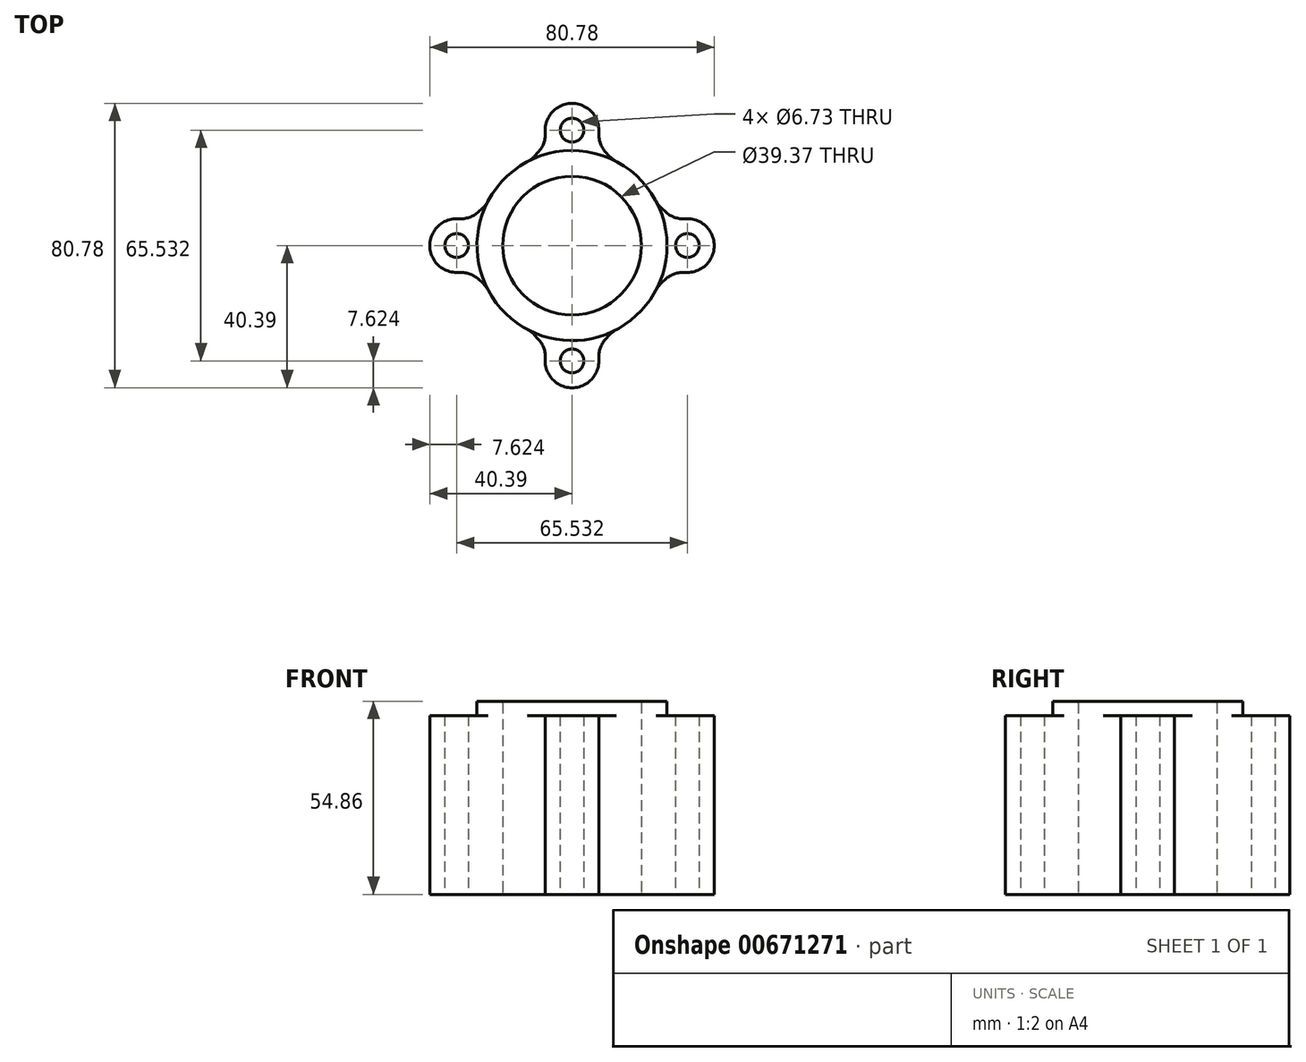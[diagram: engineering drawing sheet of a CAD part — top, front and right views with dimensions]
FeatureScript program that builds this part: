
annotation { "Feature Type Name" : "Feature", "Feature Type Description" : "" }
export const myFeature = defineFeature(function(context is Context, id is Id, definition is map)
    precondition{}
    {
        {
            var Q0;
            Q0=qCreatedBy(makeId("Top.planeOp"),FACE);
            var sketch = newSketch(context, id + "F0", { "sketchPlane" : qUnion([Q0])});
            skCircle(sketch, "E0", {"center": v(0, 0) * mm, "radius": 20.32 * mm});
            skCircle(sketch, "E1", {"center": v(0, 0) * mm, "radius": 26.99 * mm});
            skPoint(sketch, "E2", {"position": v(-32.77, 0) * mm});
            skPoint(sketch, "E3", {"position": v(32.77, 0) * mm});
            skPoint(sketch, "E4", {"position": v(0, 32.77) * mm});
            skPoint(sketch, "E5", {"position": v(0, -32.77) * mm});
            skCircle(sketch, "E6", {"center": v(-32.77, 0) * mm, "radius": 3.37 * mm});
            skCircle(sketch, "E7", {"center": v(32.77, 0) * mm, "radius": 3.37 * mm});
            skCircle(sketch, "E8", {"center": v(0, -32.77) * mm, "radius": 3.37 * mm});
            skCircle(sketch, "E9", {"center": v(0, 32.77) * mm, "radius": 3.37 * mm});
            skCircle(sketch, "E10", {"center": v(0, 32.77) * mm, "radius": 7.62 * mm});
            skCircle(sketch, "E11", {"center": v(-32.77, 0) * mm, "radius": 7.62 * mm});
            skCircle(sketch, "E12", {"center": v(0, -32.77) * mm, "radius": 7.62 * mm});
            skCircle(sketch, "E13", {"center": v(32.77, 0) * mm, "radius": 7.62 * mm});
            skPoint(sketch, "E14", {"position": v(6.87, 29.47) * mm});
            skPoint(sketch, "E15", {"position": v(11.55, 24.4) * mm});
            skPoint(sketch, "E16", {"position": v(24.4, 11.55) * mm});
            skPoint(sketch, "E17", {"position": v(29.47, 6.87) * mm});
            skLineSegment(sketch, "E18", {"start": v(6.87, 29.47) * mm, "end": v(11.55, 24.4) * mm});
            skLineSegment(sketch, "E19", {"start": v(24.4, 11.55) * mm, "end": v(29.47, 6.87) * mm});
            skPoint(sketch, "E20", {"position": v(-6.87, 29.47) * mm});
            skPoint(sketch, "E21", {"position": v(-11.55, 24.4) * mm});
            skPoint(sketch, "E22", {"position": v(-24.4, 11.55) * mm});
            skPoint(sketch, "E23", {"position": v(-29.47, 6.87) * mm});
            skPoint(sketch, "E24", {"position": v(-29.47, -6.87) * mm});
            skPoint(sketch, "E25", {"position": v(-24.4, -11.55) * mm});
            skPoint(sketch, "E26", {"position": v(-11.55, -24.4) * mm});
            skPoint(sketch, "E27", {"position": v(-6.87, -29.47) * mm});
            skPoint(sketch, "E28", {"position": v(6.87, -29.47) * mm});
            skPoint(sketch, "E29", {"position": v(11.55, -24.4) * mm});
            skPoint(sketch, "E30", {"position": v(24.4, -11.55) * mm});
            skPoint(sketch, "E31", {"position": v(29.47, -6.87) * mm});
            skLineSegment(sketch, "E32", {"start": v(-29.47, -6.87) * mm, "end": v(-24.4, -11.55) * mm});
            skLineSegment(sketch, "E33", {"start": v(-29.47, 6.87) * mm, "end": v(-24.4, 11.55) * mm});
            skLineSegment(sketch, "E34", {"start": v(-11.55, -24.4) * mm, "end": v(-6.87, -29.47) * mm});
            skLineSegment(sketch, "E35", {"start": v(6.87, -29.47) * mm, "end": v(11.55, -24.4) * mm});
            skLineSegment(sketch, "E36", {"start": v(24.4, -11.55) * mm, "end": v(29.47, -6.87) * mm});
            skLineSegment(sketch, "E37", {"start": v(-11.55, 24.4) * mm, "end": v(-6.87, 29.47) * mm});
            skSolve(sketch);
        }
        {
            var Q0;
            {var subQ0=sQuery(id+"F0.wireOp",EDGE,"E37");Q0=makeQuery(id+"F0.imprint","IMPRINT",FACE,{"disambiguationData":[TD([[makeQuery(id+"F0.imprint","IMPRINT",EDGE,{"derivedFrom":subQ0}),-1.0]])]});}
            var Q1;
            {var subQ0=sQuery(id+"F0.wireOp",EDGE,"E18");Q1=makeQuery(id+"F0.imprint","IMPRINT",FACE,{"disambiguationData":[TD([[makeQuery(id+"F0.imprint","IMPRINT",EDGE,{"derivedFrom":subQ0}),-1.0]])]});}
            var Q2;
            Q2=makeQuery(id+"F0.imprint","IMPRINT",FACE,{"disambiguationData":[TD([[makeQuery(id+"F0.imprint","IMPRINT",EDGE,{"derivedFrom":sQuery(id+"F0.wireOp",EDGE,"E9")}),-1.0]])]});
            var Q3;
            {var subQ0=sQuery(id+"F0.wireOp",EDGE,"E10");var subQ1=sQuery(id+"F0.wireOp",EDGE,"E1");var subQ2=makeQuery(id+"F0.imprint","INTERSECT",VERTEX,{"disambiguationData":[OD(0.0)],"derivedFrom":[subQ1,subQ0]});Q3=makeQuery(id+"F0.imprint","IMPRINT",FACE,{"disambiguationData":[TD([[makeQuery(id+"F0.imprint","IMPRINT",EDGE,{"disambiguationData":[TD([[subQ2,-1.0]])],"derivedFrom":subQ1}),1.0]])]});}
            var Q4;
            {var subQ0=sQuery(id+"F0.wireOp",EDGE,"E33");Q4=makeQuery(id+"F0.imprint","IMPRINT",FACE,{"disambiguationData":[TD([[makeQuery(id+"F0.imprint","IMPRINT",EDGE,{"derivedFrom":subQ0}),-1.0]])]});}
            var Q5;
            Q5=makeQuery(id+"F0.imprint","IMPRINT",FACE,{"disambiguationData":[TD([[makeQuery(id+"F0.imprint","IMPRINT",EDGE,{"derivedFrom":sQuery(id+"F0.wireOp",EDGE,"E6")}),-1.0]])]});
            var Q6;
            {var subQ0=sQuery(id+"F0.wireOp",EDGE,"E11");var subQ1=sQuery(id+"F0.wireOp",EDGE,"E1");var subQ2=makeQuery(id+"F0.imprint","INTERSECT",VERTEX,{"disambiguationData":[OD(0.0)],"derivedFrom":[subQ1,subQ0]});Q6=makeQuery(id+"F0.imprint","IMPRINT",FACE,{"disambiguationData":[TD([[makeQuery(id+"F0.imprint","IMPRINT",EDGE,{"disambiguationData":[TD([[subQ2,-1.0]])],"derivedFrom":subQ1}),1.0]])]});}
            var Q7;
            {var subQ0=sQuery(id+"F0.wireOp",EDGE,"E32");Q7=makeQuery(id+"F0.imprint","IMPRINT",FACE,{"disambiguationData":[TD([[makeQuery(id+"F0.imprint","IMPRINT",EDGE,{"derivedFrom":subQ0}),1.0]])]});}
            var Q8;
            {var subQ0=sQuery(id+"F0.wireOp",EDGE,"E34");Q8=makeQuery(id+"F0.imprint","IMPRINT",FACE,{"disambiguationData":[TD([[makeQuery(id+"F0.imprint","IMPRINT",EDGE,{"derivedFrom":subQ0}),1.0]])]});}
            var Q9;
            {var subQ0=sQuery(id+"F0.wireOp",EDGE,"E12");var subQ1=sQuery(id+"F0.wireOp",EDGE,"E1");var subQ2=makeQuery(id+"F0.imprint","INTERSECT",VERTEX,{"disambiguationData":[OD(0.0)],"derivedFrom":[subQ1,subQ0]});Q9=makeQuery(id+"F0.imprint","IMPRINT",FACE,{"disambiguationData":[TD([[makeQuery(id+"F0.imprint","IMPRINT",EDGE,{"disambiguationData":[TD([[subQ2,-1.0]])],"derivedFrom":subQ1}),1.0]])]});}
            var Q10;
            Q10=makeQuery(id+"F0.imprint","IMPRINT",FACE,{"disambiguationData":[TD([[makeQuery(id+"F0.imprint","IMPRINT",EDGE,{"derivedFrom":sQuery(id+"F0.wireOp",EDGE,"E8")}),-1.0]])]});
            var Q11;
            {var subQ0=sQuery(id+"F0.wireOp",EDGE,"E35");Q11=makeQuery(id+"F0.imprint","IMPRINT",FACE,{"disambiguationData":[TD([[makeQuery(id+"F0.imprint","IMPRINT",EDGE,{"derivedFrom":subQ0}),1.0]])]});}
            var Q12;
            {var subQ0=sQuery(id+"F0.wireOp",EDGE,"E36");Q12=makeQuery(id+"F0.imprint","IMPRINT",FACE,{"disambiguationData":[TD([[makeQuery(id+"F0.imprint","IMPRINT",EDGE,{"derivedFrom":subQ0}),1.0]])]});}
            var Q13;
            Q13=makeQuery(id+"F0.imprint","IMPRINT",FACE,{"disambiguationData":[TD([[makeQuery(id+"F0.imprint","IMPRINT",EDGE,{"derivedFrom":sQuery(id+"F0.wireOp",EDGE,"E7")}),-1.0]])]});
            var Q14;
            {var subQ0=sQuery(id+"F0.wireOp",EDGE,"E13");var subQ1=sQuery(id+"F0.wireOp",EDGE,"E1");var subQ2=makeQuery(id+"F0.imprint","INTERSECT",VERTEX,{"disambiguationData":[OD(0.0)],"derivedFrom":[subQ1,subQ0]});Q14=makeQuery(id+"F0.imprint","IMPRINT",FACE,{"disambiguationData":[TD([[makeQuery(id+"F0.imprint","IMPRINT",EDGE,{"disambiguationData":[TD([[subQ2,1.0]])],"derivedFrom":subQ1}),1.0]])]});}
            var Q15;
            {var subQ0=sQuery(id+"F0.wireOp",EDGE,"E19");Q15=makeQuery(id+"F0.imprint","IMPRINT",FACE,{"disambiguationData":[TD([[makeQuery(id+"F0.imprint","IMPRINT",EDGE,{"derivedFrom":subQ0}),-1.0]])]});}
            var Q16;
            Q16=makeQuery(id+"F0.imprint","IMPRINT",FACE,{"disambiguationData":[TD([[makeQuery(id+"F0.imprint","IMPRINT",EDGE,{"derivedFrom":sQuery(id+"F0.wireOp",EDGE,"E0")}),-1.0]])]});
            var Q17;
            {var subQ1=sQuery(id+"F0.wireOp",EDGE,"E10");var subQ3=sQuery(id+"F0.wireOp",EDGE,"E1");var subQ4=makeQuery(id+"F0.imprint","INTERSECT",VERTEX,{"disambiguationData":[OD(0.0)],"derivedFrom":[subQ3,subQ1]});Q17=makeQuery(id+"F0.imprint","IMPRINT",FACE,{"disambiguationData":[TD([[makeQuery(id+"F0.imprint","IMPRINT",EDGE,{"disambiguationData":[TD([[subQ4,-1.0]])],"derivedFrom":subQ3}),-1.0]])]});}
            var Q18;
            {var subQ1=sQuery(id+"F0.wireOp",EDGE,"E11");var subQ3=sQuery(id+"F0.wireOp",EDGE,"E1");var subQ6=makeQuery(id+"F0.imprint","INTERSECT",VERTEX,{"disambiguationData":[OD(0.0)],"derivedFrom":[subQ3,subQ1]});Q18=makeQuery(id+"F0.imprint","IMPRINT",FACE,{"disambiguationData":[TD([[makeQuery(id+"F0.imprint","IMPRINT",EDGE,{"disambiguationData":[TD([[subQ6,-1.0]])],"derivedFrom":subQ3}),-1.0]])]});}
            var Q19;
            {var subQ1=sQuery(id+"F0.wireOp",EDGE,"E13");var subQ3=sQuery(id+"F0.wireOp",EDGE,"E1");var subQ4=makeQuery(id+"F0.imprint","INTERSECT",VERTEX,{"disambiguationData":[OD(0.0)],"derivedFrom":[subQ3,subQ1]});Q19=makeQuery(id+"F0.imprint","IMPRINT",FACE,{"disambiguationData":[TD([[makeQuery(id+"F0.imprint","IMPRINT",EDGE,{"disambiguationData":[TD([[subQ4,1.0]])],"derivedFrom":subQ3}),-1.0]])]});}
            var Q20;
            {var subQ1=sQuery(id+"F0.wireOp",EDGE,"E12");var subQ3=sQuery(id+"F0.wireOp",EDGE,"E1");var subQ4=makeQuery(id+"F0.imprint","INTERSECT",VERTEX,{"disambiguationData":[OD(0.0)],"derivedFrom":[subQ3,subQ1]});Q20=makeQuery(id+"F0.imprint","IMPRINT",FACE,{"disambiguationData":[TD([[makeQuery(id+"F0.imprint","IMPRINT",EDGE,{"disambiguationData":[TD([[subQ4,-1.0]])],"derivedFrom":subQ3}),-1.0]])]});}
            extrude(context, id + "F1", {"entities" : qUnion([Q0, Q1, Q2, Q3, Q4, Q5, Q6, Q7, Q8, Q9, Q10, Q11, Q12, Q13, Q14, Q15, Q16, Q17, Q18, Q19, Q20]), "depth" : 50.8 * mm, "offsetDistance" : 25.4 * mm});
        }
        {
            var Q0;
            Q0=makeQuery(id+"F1.opExtrude","SWEPT_EDGE",EDGE,{"disambiguationData":[OSD([sQuery(id+"F0.wireOp",EDGE,"E10"),sQuery(id+"F0.wireOp",EDGE,"E37")])]});
            var Q1;
            Q1=makeQuery(id+"F1.opExtrude","SWEPT_EDGE",EDGE,{"disambiguationData":[OSD([sQuery(id+"F0.wireOp",EDGE,"E11"),sQuery(id+"F0.wireOp",EDGE,"E33")])]});
            var Q2;
            Q2=makeQuery(id+"F1.opExtrude","SWEPT_EDGE",EDGE,{"disambiguationData":[OSD([sQuery(id+"F0.wireOp",EDGE,"E11"),sQuery(id+"F0.wireOp",EDGE,"E32")])]});
            var Q3;
            Q3=makeQuery(id+"F1.opExtrude","SWEPT_EDGE",EDGE,{"disambiguationData":[OSD([sQuery(id+"F0.wireOp",EDGE,"E1"),sQuery(id+"F0.wireOp",EDGE,"E32")])]});
            var Q4;
            Q4=makeQuery(id+"F1.opExtrude","SWEPT_EDGE",EDGE,{"disambiguationData":[OSD([sQuery(id+"F0.wireOp",EDGE,"E1"),sQuery(id+"F0.wireOp",EDGE,"E34")])]});
            var Q5;
            Q5=makeQuery(id+"F1.opExtrude","SWEPT_EDGE",EDGE,{"disambiguationData":[OSD([sQuery(id+"F0.wireOp",EDGE,"E12"),sQuery(id+"F0.wireOp",EDGE,"E34")])]});
            var Q6;
            Q6=makeQuery(id+"F1.opExtrude","SWEPT_EDGE",EDGE,{"disambiguationData":[OSD([sQuery(id+"F0.wireOp",EDGE,"E12"),sQuery(id+"F0.wireOp",EDGE,"E35")])]});
            var Q7;
            Q7=makeQuery(id+"F1.opExtrude","SWEPT_EDGE",EDGE,{"disambiguationData":[OSD([sQuery(id+"F0.wireOp",EDGE,"E1"),sQuery(id+"F0.wireOp",EDGE,"E35")])]});
            var Q8;
            Q8=makeQuery(id+"F1.opExtrude","SWEPT_EDGE",EDGE,{"disambiguationData":[OSD([sQuery(id+"F0.wireOp",EDGE,"E1"),sQuery(id+"F0.wireOp",EDGE,"E36")])]});
            var Q9;
            Q9=makeQuery(id+"F1.opExtrude","SWEPT_EDGE",EDGE,{"disambiguationData":[OSD([sQuery(id+"F0.wireOp",EDGE,"E13"),sQuery(id+"F0.wireOp",EDGE,"E36")])]});
            var Q10;
            Q10=makeQuery(id+"F1.opExtrude","SWEPT_EDGE",EDGE,{"disambiguationData":[OSD([sQuery(id+"F0.wireOp",EDGE,"E13"),sQuery(id+"F0.wireOp",EDGE,"E19")])]});
            var Q11;
            Q11=makeQuery(id+"F1.opExtrude","SWEPT_EDGE",EDGE,{"disambiguationData":[OSD([sQuery(id+"F0.wireOp",EDGE,"E1"),sQuery(id+"F0.wireOp",EDGE,"E19")])]});
            var Q12;
            Q12=makeQuery(id+"F1.opExtrude","SWEPT_EDGE",EDGE,{"disambiguationData":[OSD([sQuery(id+"F0.wireOp",EDGE,"E1"),sQuery(id+"F0.wireOp",EDGE,"E18")])]});
            var Q13;
            Q13=makeQuery(id+"F1.opExtrude","SWEPT_EDGE",EDGE,{"disambiguationData":[OSD([sQuery(id+"F0.wireOp",EDGE,"E10"),sQuery(id+"F0.wireOp",EDGE,"E18")])]});
            var Q14;
            Q14=makeQuery(id+"F1.opExtrude","SWEPT_EDGE",EDGE,{"disambiguationData":[OSD([sQuery(id+"F0.wireOp",EDGE,"E1"),sQuery(id+"F0.wireOp",EDGE,"E37")])]});
            var Q15;
            Q15=makeQuery(id+"F1.opExtrude","SWEPT_EDGE",EDGE,{"disambiguationData":[OSD([sQuery(id+"F0.wireOp",EDGE,"E1"),sQuery(id+"F0.wireOp",EDGE,"E33")])]});
            fillet(context, id + "F2", {"entities" : qUnion([Q0, Q1, Q2, Q3, Q4, Q5, Q6, Q7, Q8, Q9, Q10, Q11, Q12, Q13, Q14, Q15]), "radius" : 7.62 * mm, "tangentPropagation" : true, "allowEdgeOverflow" : false});
        }
        {
            var Q0;
            Q0=qCreatedBy(makeId("Top.planeOp"),FACE);
            var sketch = newSketch(context, id + "F3", { "sketchPlane" : qUnion([Q0])});
            skCircle(sketch, "E38", {"center": v(0, 0) * mm, "radius": 19.69 * mm});
            skCircle(sketch, "E39", {"center": v(0, 0) * mm, "radius": 26.99 * mm});
            skSolve(sketch);
        }
        {
            var Q0;
            Q0=qSketchRegion(id+"F3",true);
            extrude(context, id + "F4", {"entities" : qUnion([Q0]), "operationType" : NewBodyOperationType.ADD, "depth" : 54.86 * mm, "offsetDistance" : 25.4 * mm});
        }
        {
            var Q0;
            Q0=makeQuery(id+"F4.opExtrude","CAP_EDGE",EDGE,{"disambiguationData":[OSD([sQuery(id+"F3.wireOp",EDGE,"E38")])],"isStart":false});
            var Q1;
            Q1=makeQuery(id+"F4.opExtrude","CAP_EDGE",EDGE,{"disambiguationData":[OSD([sQuery(id+"F3.wireOp",EDGE,"E38")])],"isStart":true});
            fillet(context, id + "F5", {"entities" : qUnion([Q0, Q1]), "radius" : 0.5 * mm, "tangentPropagation" : true, "allowEdgeOverflow" : false});
        }
    });
